# Revit family: DAN DRYER Stainless Design Mini Design 280 -AE - MEP
name_source: partatom
category: Furniture Systems
revit_build: Autodesk Revit 2018 (Build: 20170223_1515(x64)
units: mm (PartAtom-declared; Revit-internal decimal feet)

## family parameters
Always vertical = Yes
Cut with Voids When Loaded = No
Host = Wall
Part Type = Normal
Room Calculation Point = No
Round Connector Dimension = Use Diameter
Shared = No

## types (1)
- Stål
    Cost = 0 $
    Description = WARM-AIR HAND DRYER with IR sensor, type AE DESIGN, Art. no. 280-AE
    Height = 380 mm
    Manufacturer = http://www.dandryer.com
    Model = Stainless design
    Offset from Floor = 1500 mm  [stored 4.92126 ft]
    Type Image = <None>
    URL = http://www.dandryer.com
    Wicth = 304 mm

note: [stored X ft] marks values corroborated as IEEE doubles in the binary element streams (Revit-internal decimal feet)

## geometry (parser evidence)
native form markers: Sweep x2
no freeform markers — native parametric forms only
